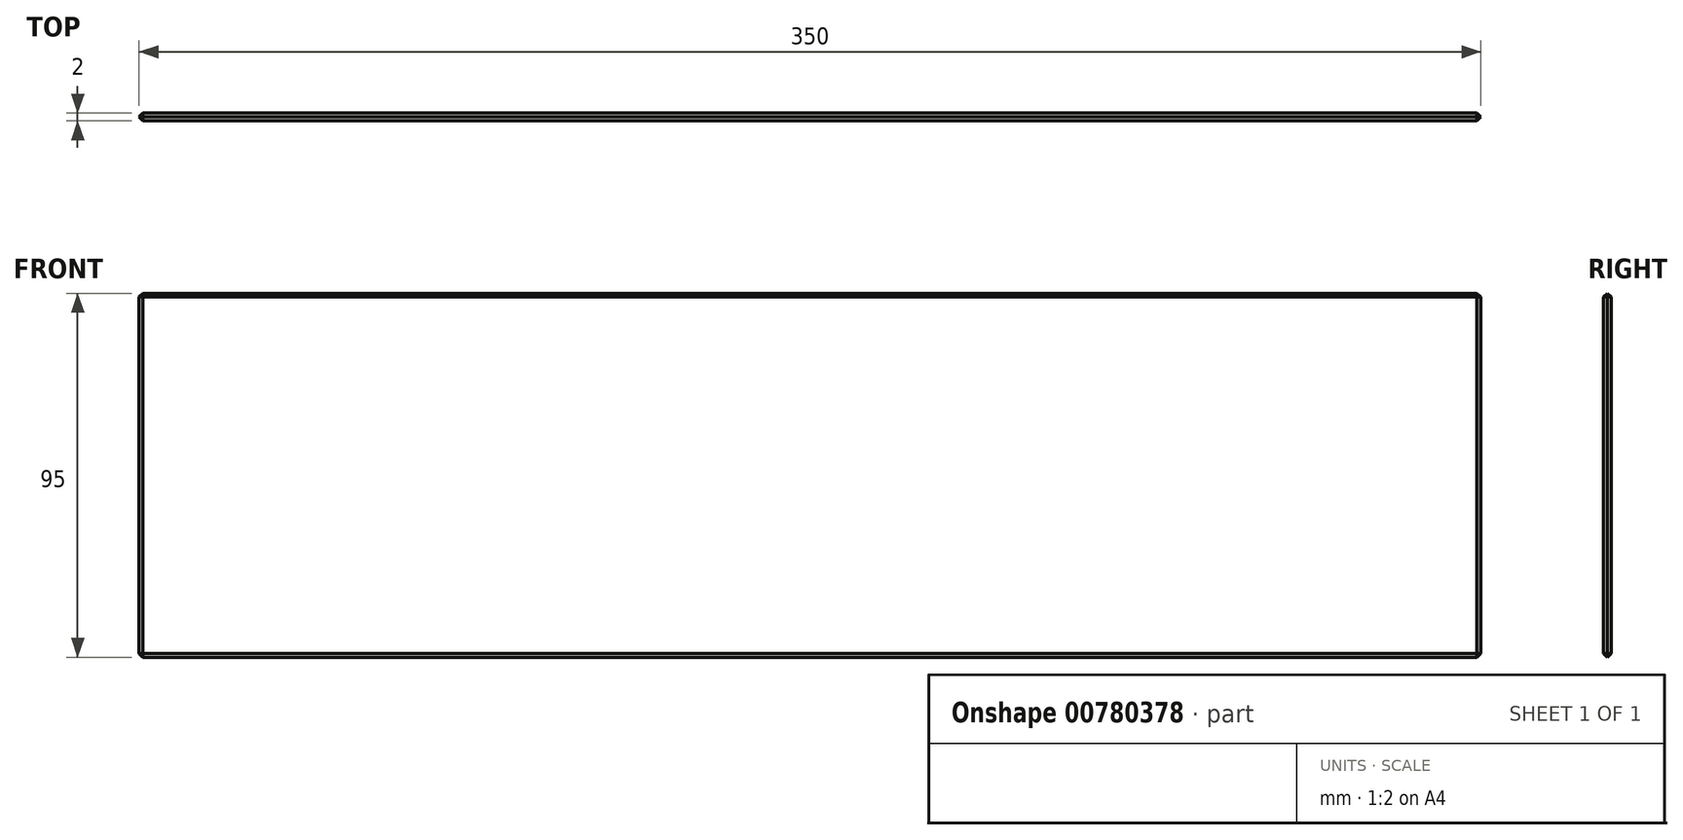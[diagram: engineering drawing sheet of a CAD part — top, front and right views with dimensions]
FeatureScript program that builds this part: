
annotation { "Feature Type Name" : "Feature", "Feature Type Description" : "" }
export const myFeature = defineFeature(function(context is Context, id is Id, definition is map)
    precondition{}
    {
        {
            var Q0;
            Q0=qCreatedBy(makeId("Front.planeOp"),FACE);
            var sketch = newSketch(context, id + "F0", { "sketchPlane" : qUnion([Q0])});
            skLineSegment(sketch, "E0.bottom", {"start": v(-175, 47.5) * mm, "end": v(175, 47.5) * mm});
            skLineSegment(sketch, "E0.top", {"start": v(-175, -47.5) * mm, "end": v(175, -47.5) * mm});
            skLineSegment(sketch, "E0.left", {"start": v(-175, 47.5) * mm, "end": v(-175, -47.5) * mm});
            skLineSegment(sketch, "E0.right", {"start": v(175, 47.5) * mm, "end": v(175, -47.5) * mm});
            skPoint(sketch, "E0.middle", {"position": v(0, 0) * mm});
            skSolve(sketch);
        }
        {
            var Q0;
            Q0=makeQuery(id+"F0.imprint","IMPRINT",FACE,{"disambiguationData":[TD([[makeQuery(id+"F0.imprint","IMPRINT",EDGE,{"derivedFrom":sQuery(id+"F0.wireOp",EDGE,"E0.bottom")}),-1.0]])]});
            extrude(context, id + "F1", {"entities" : qUnion([Q0]), "depth" : 2 * mm, "offsetDistance" : 25 * mm});
        }
        {
            var Q0;
            Q0=makeQuery(id+"F1.opExtrude","CAP_EDGE",EDGE,{"disambiguationData":[OSD([sQuery(id+"F0.wireOp",EDGE,"E0.left")])],"isStart":true});
            var Q1;
            Q1=makeQuery(id+"F1.opExtrude","CAP_EDGE",EDGE,{"disambiguationData":[OSD([sQuery(id+"F0.wireOp",EDGE,"E0.bottom")])],"isStart":true});
            var Q2;
            Q2=makeQuery(id+"F1.opExtrude","CAP_EDGE",EDGE,{"disambiguationData":[OSD([sQuery(id+"F0.wireOp",EDGE,"E0.bottom")])],"isStart":false});
            var Q3;
            Q3=makeQuery(id+"F1.opExtrude","CAP_EDGE",EDGE,{"disambiguationData":[OSD([sQuery(id+"F0.wireOp",EDGE,"E0.left")])],"isStart":false});
            var Q4;
            Q4=makeQuery(id+"F1.opExtrude","CAP_EDGE",EDGE,{"disambiguationData":[OSD([sQuery(id+"F0.wireOp",EDGE,"E0.right")])],"isStart":true});
            var Q5;
            Q5=makeQuery(id+"F1.opExtrude","CAP_EDGE",EDGE,{"disambiguationData":[OSD([sQuery(id+"F0.wireOp",EDGE,"E0.top")])],"isStart":true});
            var Q6;
            Q6=makeQuery(id+"F1.opExtrude","CAP_EDGE",EDGE,{"disambiguationData":[OSD([sQuery(id+"F0.wireOp",EDGE,"E0.top")])],"isStart":false});
            var Q7;
            Q7=makeQuery(id+"F1.opExtrude","CAP_EDGE",EDGE,{"disambiguationData":[OSD([sQuery(id+"F0.wireOp",EDGE,"E0.right")])],"isStart":false});
            var Q8;
            Q8=makeQuery(id+"F1.opExtrude","SWEPT_EDGE",EDGE,{"disambiguationData":[OSD([sQuery(id+"F0.wireOp",EDGE,"E0.top"),sQuery(id+"F0.wireOp",EDGE,"E0.right")])]});
            var Q9;
            Q9=makeQuery(id+"F1.opExtrude","SWEPT_EDGE",EDGE,{"disambiguationData":[OSD([sQuery(id+"F0.wireOp",EDGE,"E0.bottom"),sQuery(id+"F0.wireOp",EDGE,"E0.right")])]});
            var Q10;
            Q10=makeQuery(id+"F1.opExtrude","SWEPT_EDGE",EDGE,{"disambiguationData":[OSD([sQuery(id+"F0.wireOp",EDGE,"E0.bottom"),sQuery(id+"F0.wireOp",EDGE,"E0.left")])]});
            var Q11;
            Q11=makeQuery(id+"F1.opExtrude","SWEPT_EDGE",EDGE,{"disambiguationData":[OSD([sQuery(id+"F0.wireOp",EDGE,"E0.top"),sQuery(id+"F0.wireOp",EDGE,"E0.left")])]});
            chamfer(context, id + "F2", {"entities" : qUnion([Q0, Q1, Q2, Q3, Q4, Q5, Q6, Q7, Q8, Q9, Q10, Q11]), "width" : 1 * mm, "tangentPropagation" : true});
        }
    });
